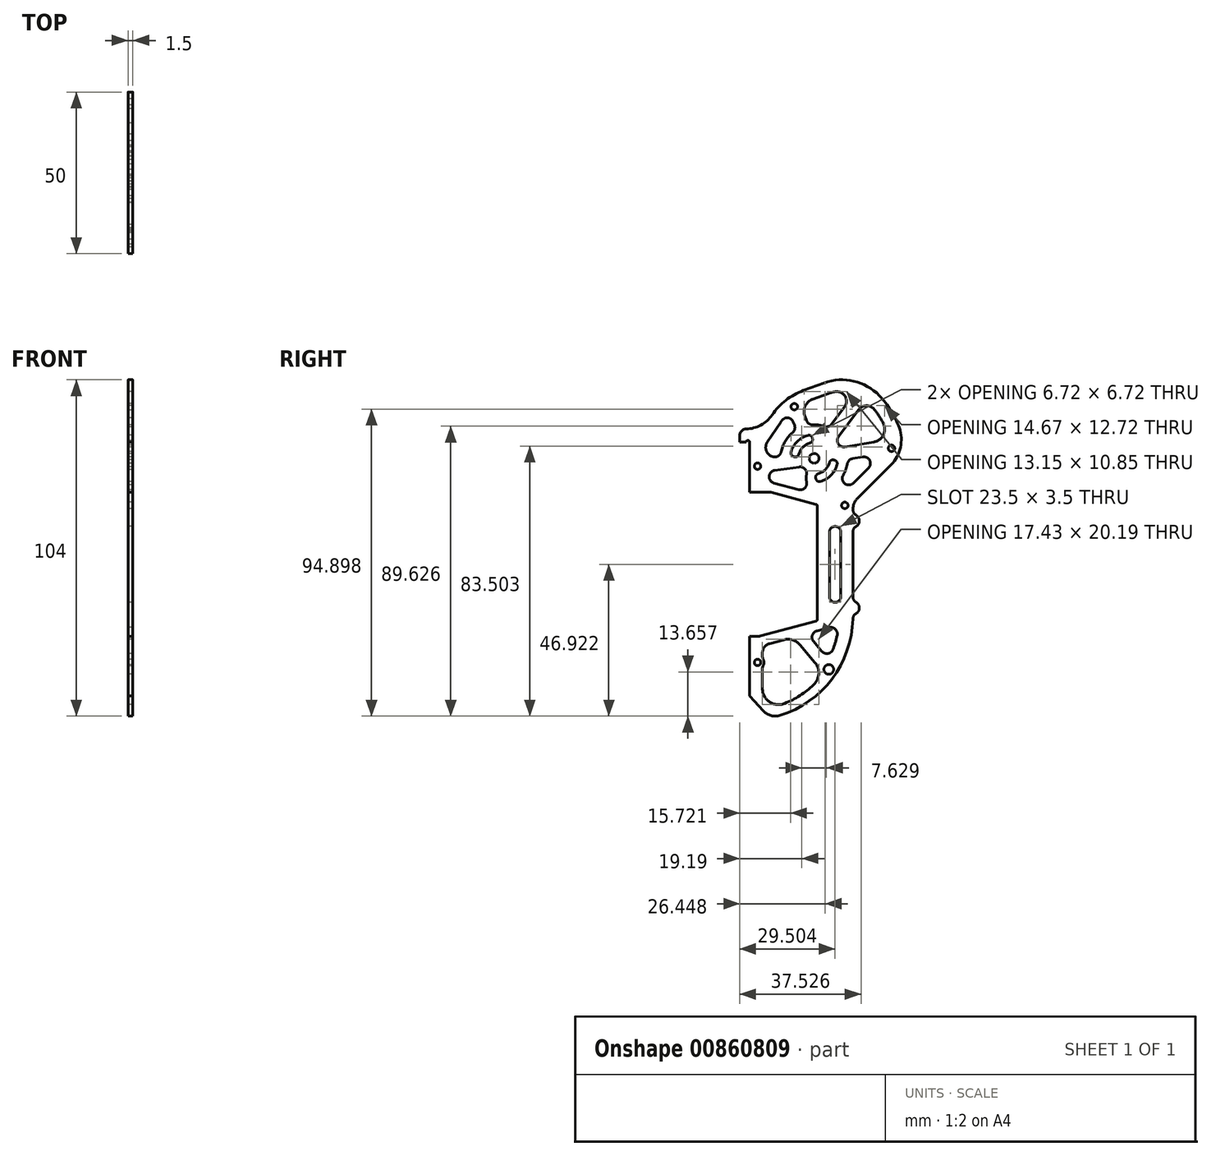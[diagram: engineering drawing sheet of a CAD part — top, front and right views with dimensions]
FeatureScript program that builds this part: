
annotation { "Feature Type Name" : "Feature", "Feature Type Description" : "" }
export const myFeature = defineFeature(function(context is Context, id is Id, definition is map)
    precondition{}
    {
        {
            var Q0;
            Q0=qCreatedBy(makeId("Right.planeOp"),FACE);
            var sketch = newSketch(context, id + "F0", { "sketchPlane" : qUnion([Q0])});
            skCircle(sketch, "E0", {"center": v(-19.5, -35.42) * mm, "radius": 1 * mm});
            skArc(sketch, "E1", {"start": v(9.9, 27.61) * mm, "mid": v(8.82, 27.06) * mm, "end": v(8.26, 25.97) * mm});
            skArc(sketch, "E2", {"start": v(8.26, 25.97) * mm, "mid": v(7.8, 24.17) * mm, "end": v(7, 22.48) * mm});
            skArc(sketch, "E3", {"start": v(7, 22.48) * mm, "mid": v(7.52, 19.9) * mm, "end": v(10.15, 20.06) * mm});
            skLineSegment(sketch, "E4", {"start": v(10.15, 20.06) * mm, "end": v(14.84, 24.75) * mm});
            skArc(sketch, "E5", {"start": v(14.84, 24.75) * mm, "mid": v(15.2, 27.08) * mm, "end": v(13.1, 28.14) * mm});
            skLineSegment(sketch, "E6", {"start": v(13.1, 28.14) * mm, "end": v(9.9, 27.61) * mm});
            skArc(sketch, "E7", {"start": v(16.58, 42.89) * mm, "mid": v(18.13, 40.77) * mm, "end": v(19.43, 38.5) * mm});
            skArc(sketch, "E8", {"start": v(19.43, 38.5) * mm, "mid": v(19.43, 34.88) * mm, "end": v(16.5, 32.75) * mm});
            skLineSegment(sketch, "E9", {"start": v(16.5, 32.75) * mm, "end": v(7.51, 31.27) * mm});
            skArc(sketch, "E10", {"start": v(7.51, 31.27) * mm, "mid": v(5.48, 32.21) * mm, "end": v(5.59, 34.45) * mm});
            skLineSegment(sketch, "E11", {"start": v(5.59, 34.45) * mm, "end": v(11.86, 42.79) * mm});
            skArc(sketch, "E12", {"start": v(11.86, 42.79) * mm, "mid": v(14.2, 43.99) * mm, "end": v(16.58, 42.89) * mm});
            skCircle(sketch, "E13", {"center": v(-19.5, 25.28) * mm, "radius": 1 * mm});
            skCircle(sketch, "E14", {"center": v(-8.12, 43.69) * mm, "radius": 1 * mm});
            skArc(sketch, "E15", {"start": v(-17.75, -34.45) * mm, "mid": v(-17.5, -35.42) * mm, "end": v(-17.75, -36.39) * mm});
            skArc(sketch, "E16", {"start": v(-17.75, -36.39) * mm, "mid": v(-17.93, -36.86) * mm, "end": v(-18, -37.36) * mm});
            skLineSegment(sketch, "E17", {"start": v(-18, -37.36) * mm, "end": v(-18, -43.47) * mm});
            skArc(sketch, "E18", {"start": v(-18, -43.47) * mm, "mid": v(-15.8, -47.61) * mm, "end": v(-11.12, -48.1) * mm});
            skArc(sketch, "E19", {"start": v(-11.12, -48.1) * mm, "mid": v(-6.36, -45.64) * mm, "end": v(-2.13, -42.34) * mm});
            skArc(sketch, "E20", {"start": v(-2.13, -42.34) * mm, "mid": v(-0.56, -39) * mm, "end": v(-1.72, -35.49) * mm});
            skLineSegment(sketch, "E21", {"start": v(-1.72, -35.49) * mm, "end": v(-6.3, -30.03) * mm});
            skArc(sketch, "E22", {"start": v(-6.3, -30.03) * mm, "mid": v(-8.63, -28.48) * mm, "end": v(-11.42, -28.42) * mm});
            skLineSegment(sketch, "E23", {"start": v(-11.42, -28.42) * mm, "end": v(-15.77, -29.58) * mm});
            skArc(sketch, "E24", {"start": v(-15.77, -29.58) * mm, "mid": v(-17.38, -30.65) * mm, "end": v(-18, -32.48) * mm});
            skLineSegment(sketch, "E25", {"start": v(-18, -32.48) * mm, "end": v(-18, -33.48) * mm});
            skArc(sketch, "E26", {"start": v(-18, -33.48) * mm, "mid": v(-17.93, -33.98) * mm, "end": v(-17.75, -34.45) * mm});
            skCircle(sketch, "E27", {"center": v(21.96, 30.81) * mm, "radius": 1 * mm});
            skCircle(sketch, "E28", {"center": v(7.5, 13.15) * mm, "radius": 1 * mm});
            skLineSegment(sketch, "E29", {"start": v(-22, -45.81) * mm, "end": v(-17.62, -50.44) * mm});
            skArc(sketch, "E30", {"start": v(-17.62, -50.44) * mm, "mid": v(-15.26, -51.84) * mm, "end": v(-12.5, -51.78) * mm});
            skArc(sketch, "E31", {"start": v(-12.5, -51.78) * mm, "mid": v(3.55, -40.5) * mm, "end": v(10, -21.97) * mm});
            skArc(sketch, "E32", {"start": v(10, -21.97) * mm, "mid": v(10.28, -20.99) * mm, "end": v(11, -20.28) * mm});
            skArc(sketch, "E33", {"start": v(11, -20.28) * mm, "mid": v(12, -18.55) * mm, "end": v(11, -16.81) * mm});
            skArc(sketch, "E34", {"start": v(11, -16.81) * mm, "mid": v(10.27, -16.08) * mm, "end": v(10, -15.08) * mm});
            skLineSegment(sketch, "E35", {"start": v(10, -15.08) * mm, "end": v(10, 4.92) * mm});
            skArc(sketch, "E36", {"start": v(10, 4.92) * mm, "mid": v(10.27, 5.92) * mm, "end": v(11, 6.65) * mm});
            skArc(sketch, "E37", {"start": v(11, 6.65) * mm, "mid": v(12, 8.39) * mm, "end": v(11, 10.12) * mm});
            skArc(sketch, "E38", {"start": v(11, 10.12) * mm, "mid": v(10.27, 10.85) * mm, "end": v(10, 11.86) * mm});
            skArc(sketch, "E39", {"start": v(10, 11.86) * mm, "mid": v(10.39, 13.76) * mm, "end": v(11.47, 15.37) * mm});
            skLineSegment(sketch, "E40", {"start": v(11.47, 15.37) * mm, "end": v(21.77, 25.68) * mm});
            skArc(sketch, "E41", {"start": v(21.77, 25.68) * mm, "mid": v(24.73, 31.06) * mm, "end": v(24.34, 37.19) * mm});
            skArc(sketch, "E42", {"start": v(24.34, 37.19) * mm, "mid": v(21.8, 42.46) * mm, "end": v(18.2, 47.09) * mm});
            skArc(sketch, "E43", {"start": v(18.2, 47.09) * mm, "mid": v(10.28, 51.59) * mm, "end": v(1.18, 51.04) * mm});
            skLineSegment(sketch, "E44", {"start": v(1.18, 51.04) * mm, "end": v(-5.28, 48.68) * mm});
            skArc(sketch, "E45", {"start": v(-5.28, 48.68) * mm, "mid": v(-10.72, 45.68) * mm, "end": v(-14.97, 41.15) * mm});
            skArc(sketch, "E46", {"start": v(-14.97, 41.15) * mm, "mid": v(-18.47, 37.99) * mm, "end": v(-23.04, 36.78) * mm});
            skArc(sketch, "E47", {"start": v(-23.04, 36.78) * mm, "mid": v(-24.42, 36.18) * mm, "end": v(-25, 34.78) * mm});
            skLineSegment(sketch, "E48", {"start": v(-25, 34.78) * mm, "end": v(-25, 32.78) * mm});
            skLineSegment(sketch, "E49", {"start": v(-25, 32.78) * mm, "end": v(-23, 32.78) * mm});
            skArc(sketch, "E50", {"start": v(-23, 32.78) * mm, "mid": v(-22.5, 33.28) * mm, "end": v(-22, 32.78) * mm});
            skLineSegment(sketch, "E51", {"start": v(-22, 32.78) * mm, "end": v(-22, 17.28) * mm});
            skLineSegment(sketch, "E52", {"start": v(-22, 17.28) * mm, "end": v(-15.83, 17.28) * mm});
            skArc(sketch, "E53", {"start": v(-15.83, 17.28) * mm, "mid": v(-15.57, 17.26) * mm, "end": v(-15.31, 17.21) * mm});
            skLineSegment(sketch, "E54", {"start": v(-15.31, 17.21) * mm, "end": v(-1.37, 13.47) * mm});
            skArc(sketch, "E55", {"start": v(-1.37, 13.47) * mm, "mid": v(-1.1, 13.3) * mm, "end": v(-1, 13) * mm});
            skLineSegment(sketch, "E56", {"start": v(-1, 13) * mm, "end": v(-1, -22.13) * mm});
            skArc(sketch, "E57", {"start": v(-1, -22.13) * mm, "mid": v(-1.1, -22.44) * mm, "end": v(-1.37, -22.62) * mm});
            skLineSegment(sketch, "E58", {"start": v(-1.37, -22.62) * mm, "end": v(-18.67, -27.25) * mm});
            skArc(sketch, "E59", {"start": v(-18.67, -27.25) * mm, "mid": v(-18.93, -27.3) * mm, "end": v(-19.19, -27.32) * mm});
            skLineSegment(sketch, "E60", {"start": v(-19.19, -27.32) * mm, "end": v(-22, -27.32) * mm});
            skLineSegment(sketch, "E61", {"start": v(-22, -27.32) * mm, "end": v(-22, -45.81) * mm});
            skCircle(sketch, "E62", {"center": v(2.55, -37.58) * mm, "radius": 1.5 * mm});
            skLineSegment(sketch, "E63", {"start": v(2.75, 4.92) * mm, "end": v(2.75, -15.08) * mm});
            skArc(sketch, "E64", {"start": v(2.75, -15.08) * mm, "mid": v(4.5, -16.83) * mm, "end": v(6.25, -15.08) * mm});
            skLineSegment(sketch, "E65", {"start": v(6.25, -15.08) * mm, "end": v(6.25, 4.92) * mm});
            skArc(sketch, "E66", {"start": v(6.25, 4.92) * mm, "mid": v(4.5, 6.67) * mm, "end": v(2.75, 4.92) * mm});
            skLineSegment(sketch, "E67", {"start": v(-2.18, -28.88) * mm, "end": v(0.42, -31.97) * mm});
            skArc(sketch, "E68", {"start": v(0.42, -31.97) * mm, "mid": v(2.27, -32.66) * mm, "end": v(3.8, -31.42) * mm});
            skArc(sketch, "E69", {"start": v(3.8, -31.42) * mm, "mid": v(4.57, -29.23) * mm, "end": v(5.15, -26.99) * mm});
            skArc(sketch, "E70", {"start": v(5.15, -26.99) * mm, "mid": v(4.57, -25.12) * mm, "end": v(2.67, -24.64) * mm});
            skLineSegment(sketch, "E71", {"start": v(2.67, -24.64) * mm, "end": v(-1.16, -25.67) * mm});
            skArc(sketch, "E72", {"start": v(-1.16, -25.67) * mm, "mid": v(-2.55, -27) * mm, "end": v(-2.18, -28.88) * mm});
            skCircle(sketch, "E73", {"center": v(-2, 27.69) * mm, "radius": 1.5 * mm});
            skArc(sketch, "E74", {"start": v(-9.13, 29.6) * mm, "mid": v(-7.22, 32.91) * mm, "end": v(-3.9, 34.83) * mm});
            skArc(sketch, "E75", {"start": v(-3.9, 34.83) * mm, "mid": v(-3.07, 34.72) * mm, "end": v(-2.56, 34.05) * mm});
            skLineSegment(sketch, "E76", {"start": v(-2.56, 34.05) * mm, "end": v(-2.49, 33.77) * mm});
            skArc(sketch, "E77", {"start": v(-2.49, 33.77) * mm, "mid": v(-2.6, 32.93) * mm, "end": v(-3.26, 32.42) * mm});
            skArc(sketch, "E78", {"start": v(-3.26, 32.42) * mm, "mid": v(-5.46, 31.15) * mm, "end": v(-6.73, 28.96) * mm});
            skArc(sketch, "E79", {"start": v(-6.73, 28.96) * mm, "mid": v(-7.24, 28.29) * mm, "end": v(-8.08, 28.18) * mm});
            skLineSegment(sketch, "E80", {"start": v(-8.08, 28.18) * mm, "end": v(-8.36, 28.25) * mm});
            skArc(sketch, "E81", {"start": v(-8.36, 28.25) * mm, "mid": v(-9.02, 28.77) * mm, "end": v(-9.13, 29.6) * mm});
            skArc(sketch, "E82", {"start": v(-1.5, 21.6) * mm, "mid": v(-1.4, 22.44) * mm, "end": v(-0.73, 22.96) * mm});
            skArc(sketch, "E83", {"start": v(-0.73, 22.96) * mm, "mid": v(1.47, 24.22) * mm, "end": v(2.74, 26.42) * mm});
            skArc(sketch, "E84", {"start": v(2.74, 26.42) * mm, "mid": v(3.25, 27.09) * mm, "end": v(4.08, 27.2) * mm});
            skLineSegment(sketch, "E85", {"start": v(4.08, 27.2) * mm, "end": v(4.36, 27.12) * mm});
            skArc(sketch, "E86", {"start": v(4.36, 27.12) * mm, "mid": v(5.03, 26.61) * mm, "end": v(5.14, 25.78) * mm});
            skArc(sketch, "E87", {"start": v(5.14, 25.78) * mm, "mid": v(3.23, 22.46) * mm, "end": v(-0.08, 20.55) * mm});
            skArc(sketch, "E88", {"start": v(-0.08, 20.55) * mm, "mid": v(-0.92, 20.66) * mm, "end": v(-1.43, 21.33) * mm});
            skLineSegment(sketch, "E89", {"start": v(-1.43, 21.33) * mm, "end": v(-1.5, 21.6) * mm});
            skArc(sketch, "E90", {"start": v(-16.44, 32.77) * mm, "mid": v(-16.73, 29.95) * mm, "end": v(-14.56, 28.15) * mm});
            skArc(sketch, "E91", {"start": v(-14.56, 28.15) * mm, "mid": v(-13.05, 28.44) * mm, "end": v(-12.2, 29.72) * mm});
            skArc(sketch, "E92", {"start": v(-12.2, 29.72) * mm, "mid": v(-10.93, 33) * mm, "end": v(-8.65, 35.68) * mm});
            skArc(sketch, "E93", {"start": v(-8.65, 35.68) * mm, "mid": v(-8, 36.71) * mm, "end": v(-8.06, 37.93) * mm});
            skLineSegment(sketch, "E94", {"start": v(-8.06, 37.93) * mm, "end": v(-8.45, 38.96) * mm});
            skArc(sketch, "E95", {"start": v(-8.45, 38.96) * mm, "mid": v(-10.06, 40.23) * mm, "end": v(-11.94, 39.42) * mm});
            skArc(sketch, "E96", {"start": v(-11.94, 39.42) * mm, "mid": v(-12.15, 39.13) * mm, "end": v(-12.35, 38.84) * mm});
            skLineSegment(sketch, "E97", {"start": v(-12.35, 38.84) * mm, "end": v(-16.44, 32.77) * mm});
            skLineSegment(sketch, "E98", {"start": v(2.4, 47.74) * mm, "end": v(-2.5, 45.96) * mm});
            skArc(sketch, "E99", {"start": v(-2.5, 45.96) * mm, "mid": v(-4.77, 43.86) * mm, "end": v(-4.86, 40.77) * mm});
            skLineSegment(sketch, "E100", {"start": v(-4.86, 40.77) * mm, "end": v(-4.33, 39.36) * mm});
            skArc(sketch, "E101", {"start": v(-4.33, 39.36) * mm, "mid": v(-3.56, 38.41) * mm, "end": v(-2.38, 38.08) * mm});
            skArc(sketch, "E102", {"start": v(-2.38, 38.08) * mm, "mid": v(-0.55, 37.99) * mm, "end": v(1.24, 37.57) * mm});
            skArc(sketch, "E103", {"start": v(1.24, 37.57) * mm, "mid": v(2.46, 37.57) * mm, "end": v(3.46, 38.27) * mm});
            skLineSegment(sketch, "E104", {"start": v(3.46, 38.27) * mm, "end": v(7.42, 43.54) * mm});
            skArc(sketch, "E105", {"start": v(7.42, 43.54) * mm, "mid": v(7.58, 46.91) * mm, "end": v(4.5, 48.3) * mm});
            skArc(sketch, "E106", {"start": v(4.5, 48.3) * mm, "mid": v(3.44, 48.06) * mm, "end": v(2.4, 47.74) * mm});
            skLineSegment(sketch, "E107", {"start": v(-14.43, 20.08) * mm, "end": v(-6.77, 18.03) * mm});
            skArc(sketch, "E108", {"start": v(-6.77, 18.03) * mm, "mid": v(-4.83, 18.55) * mm, "end": v(-4.32, 20.5) * mm});
            skArc(sketch, "E109", {"start": v(-4.32, 20.5) * mm, "mid": v(-4.48, 21.54) * mm, "end": v(-4.36, 22.58) * mm});
            skArc(sketch, "E110", {"start": v(-4.36, 22.58) * mm, "mid": v(-4.82, 24.4) * mm, "end": v(-6.58, 25.04) * mm});
            skLineSegment(sketch, "E111", {"start": v(-6.58, 25.04) * mm, "end": v(-14.18, 24) * mm});
            skArc(sketch, "E112", {"start": v(-14.18, 24) * mm, "mid": v(-15.9, 22.14) * mm, "end": v(-14.43, 20.08) * mm});
            skSolve(sketch);
        }
        {
            var Q0;
            Q0 = qSketchRegion(id + "F0", true);
            extrude(context, id + "F1", {"entities" : qUnion([Q0]), "depth" : 1.5 * mm, "offsetDistance" : 25 * mm});
        }
    });
